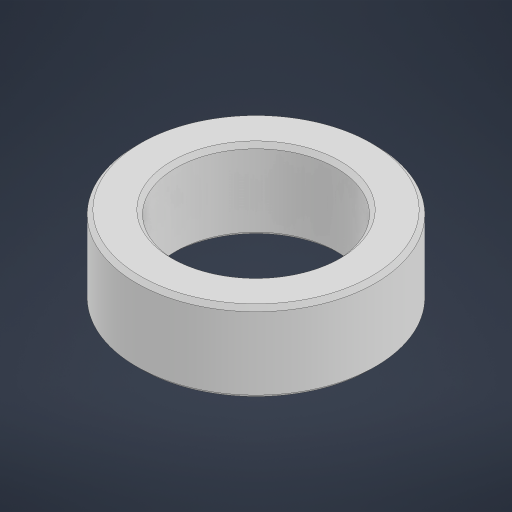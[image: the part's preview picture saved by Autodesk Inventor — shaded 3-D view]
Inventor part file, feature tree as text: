
AUTODESK INVENTOR PART (.ipt)
format: ipt  version: 2023 (Build 270158000, 158)  size: 182,784 bytes
history: native  units: in
note: dims shown in document units (in); Inventor stores cm internally (conversion verified against a paired STEP export)
features: chamfer x1
ambient origin geometry x8: Origin, YZ Plane, XZ Plane, XY Plane, X Axis, Y Axis, Z Axis, Center Point
bodies: Solid1 (feature_tree)
feature tree (1):
  chamfer  "Chamfer1"  [1 undecoded]
note: 1 required parameter value undecoded (feature->parameter linkage not recoverable at this tier; creation-order binding heuristic only, values carry confidence <= 0.55)
